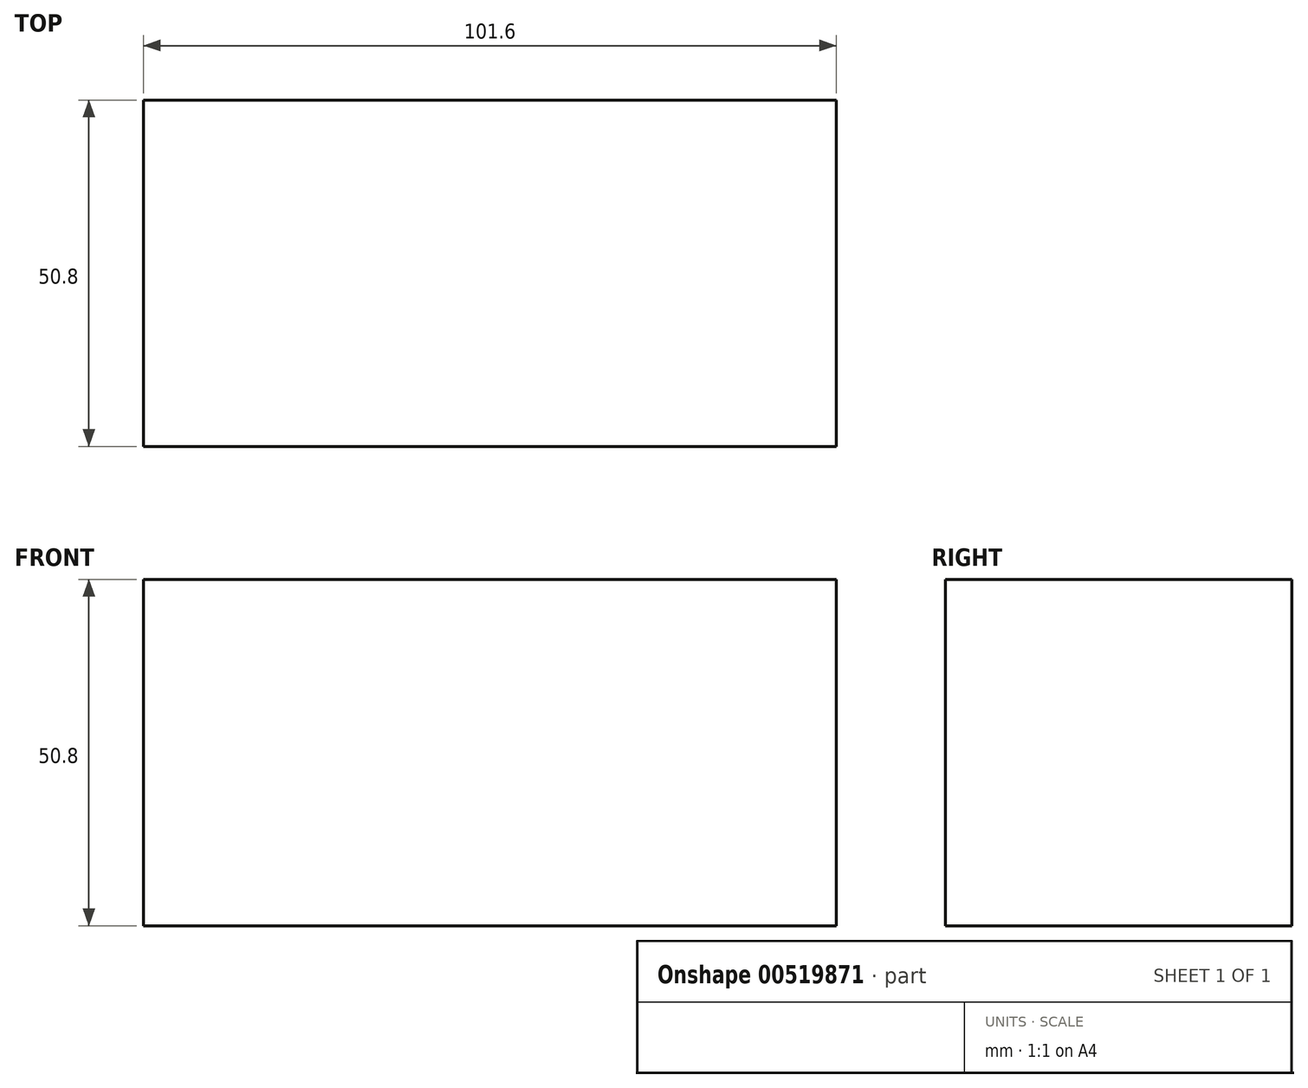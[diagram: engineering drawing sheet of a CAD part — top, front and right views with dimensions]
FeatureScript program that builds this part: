
annotation { "Feature Type Name" : "Feature", "Feature Type Description" : "" }
export const myFeature = defineFeature(function(context is Context, id is Id, definition is map)
    precondition{}
    {
        {
            var Q0;
            Q0=qCreatedBy(makeId("Top.planeOp"),FACE);
            var sketch = newSketch(context, id + "F0", { "sketchPlane" : qUnion([Q0])});
            skLineSegment(sketch, "E0.bottom", {"start": v(-13.95, 42.04) * mm, "end": v(87.65, 42.04) * mm});
            skLineSegment(sketch, "E0.top", {"start": v(-13.95, -8.76) * mm, "end": v(87.65, -8.76) * mm});
            skLineSegment(sketch, "E0.left", {"start": v(-13.95, 42.04) * mm, "end": v(-13.95, -8.76) * mm});
            skLineSegment(sketch, "E0.right", {"start": v(87.65, 42.04) * mm, "end": v(87.65, -8.76) * mm});
            skSolve(sketch);
        }
        {
            var Q0;
            Q0 = qSketchRegion(id + "F0", true);
            extrude(context, id + "F1", {"entities" : qUnion([Q0]), "depth" : 50.8 * mm, "offsetDistance" : 25.4 * mm});
        }
    });
